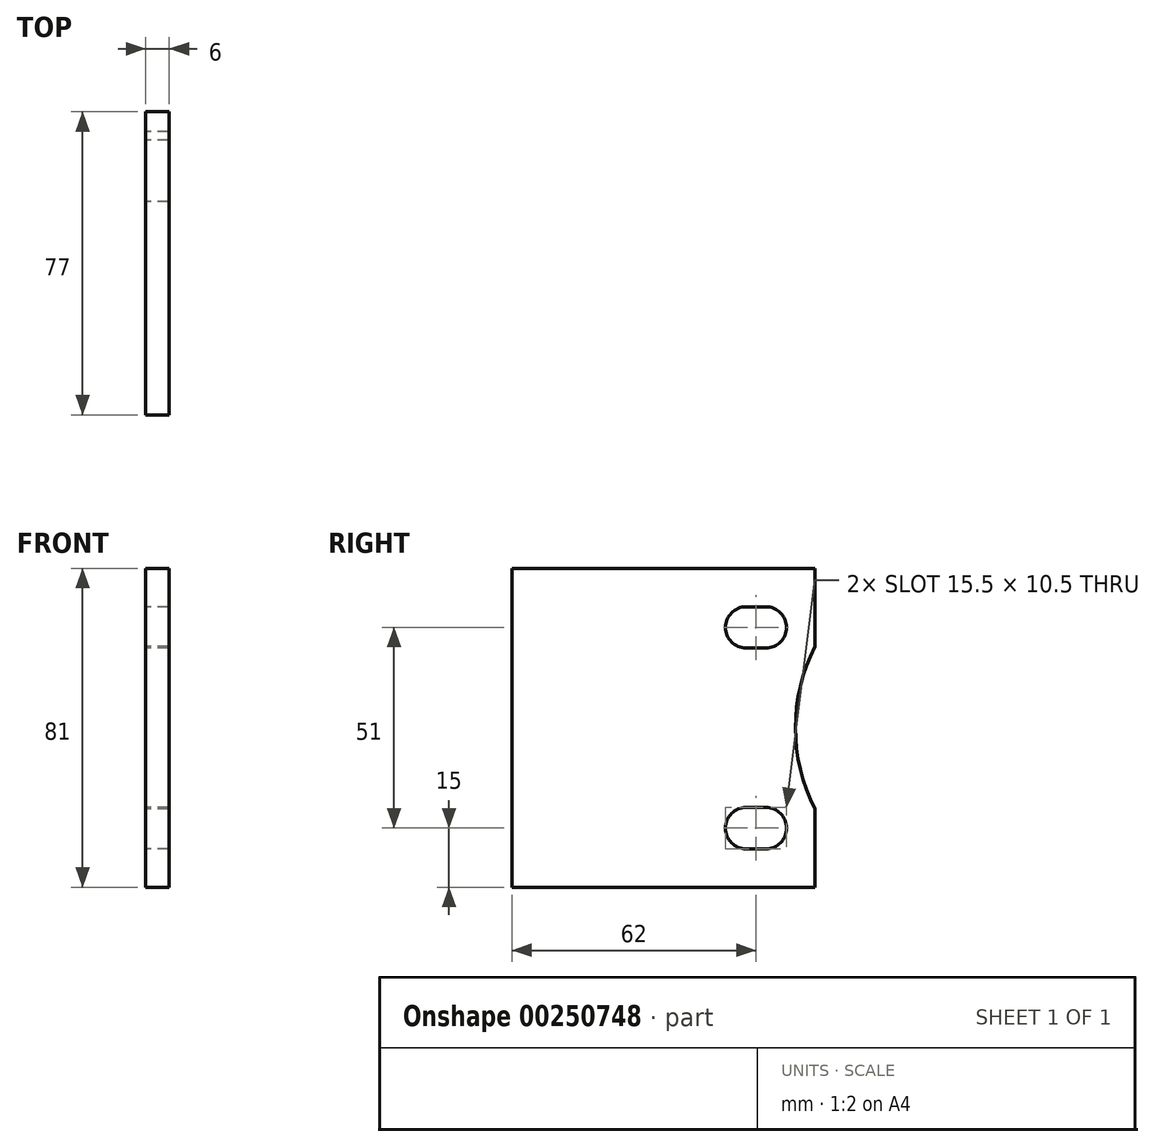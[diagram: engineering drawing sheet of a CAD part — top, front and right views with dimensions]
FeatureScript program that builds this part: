
annotation { "Feature Type Name" : "Feature", "Feature Type Description" : "" }
export const myFeature = defineFeature(function(context is Context, id is Id, definition is map)
    precondition{}
    {
        {
            var Q0;
            Q0=qCreatedBy(makeId("Right.planeOp"),FACE);
            var sketch = newSketch(context, id + "F0", { "sketchPlane" : qUnion([Q0])});
            skLineSegment(sketch, "E0.bottom", {"start": v(38.5, 40.5) * mm, "end": v(-38.5, 40.5) * mm});
            skLineSegment(sketch, "E0.top", {"start": v(38.5, -40.5) * mm, "end": v(-38.5, -40.5) * mm});
            skLineSegment(sketch, "E0.left", {"start": v(38.5, 40.5) * mm, "end": v(38.5, 20.62) * mm});
            skLineSegment(sketch, "E0.right", {"start": v(-38.5, 40.5) * mm, "end": v(-38.5, -40.5) * mm});
            skPoint(sketch, "E0.middle", {"position": v(0, 0) * mm});
            skLineSegment(sketch, "E1", {"start": v(23.5, 25.5) * mm, "end": v(23.5, -25.5) * mm, "construction": true});
            skArc(sketch, "E2", {"start": v(21, 30.75) * mm, "mid": v(15.75, 25.5) * mm, "end": v(21, 20.25) * mm});
            skArc(sketch, "E3", {"start": v(26, 20.25) * mm, "mid": v(31.25, 25.5) * mm, "end": v(26, 30.75) * mm});
            skLineSegment(sketch, "E4", {"start": v(21, 25.5) * mm, "end": v(26, 25.5) * mm, "construction": true});
            skLineSegment(sketch, "E5", {"start": v(21, 30.75) * mm, "end": v(26, 30.75) * mm});
            skLineSegment(sketch, "E6", {"start": v(21, 20.25) * mm, "end": v(26, 20.25) * mm});
            skArc(sketch, "E7", {"start": v(21, -20.25) * mm, "mid": v(15.75, -25.5) * mm, "end": v(21, -30.75) * mm});
            skArc(sketch, "E8", {"start": v(26, -30.75) * mm, "mid": v(31.25, -25.5) * mm, "end": v(26, -20.25) * mm});
            skLineSegment(sketch, "E9", {"start": v(21, -25.5) * mm, "end": v(26, -25.5) * mm, "construction": true});
            skLineSegment(sketch, "E10", {"start": v(21, -20.25) * mm, "end": v(26, -20.25) * mm});
            skLineSegment(sketch, "E11", {"start": v(21, -30.75) * mm, "end": v(26, -30.75) * mm});
            skPoint(sketch, "E12", {"position": v(23.5, 25.5) * mm});
            skPoint(sketch, "E13", {"position": v(23.5, -25.5) * mm});
            skArc(sketch, "E14", {"start": v(38.5, 20.62) * mm, "mid": v(33.5, 0) * mm, "end": v(38.5, -20.62) * mm});
            skLineSegment(sketch, "E15.trimOffspring", {"start": v(38.5, -20.62) * mm, "end": v(38.5, -40.5) * mm});
            skSolve(sketch);
        }
        {
            var Q0;
            Q0=qSketchRegion(id+"F0",true);
            extrude(context, id + "F1", {"entities" : qUnion([Q0]), "depth" : 6 * mm});
        }
    });
